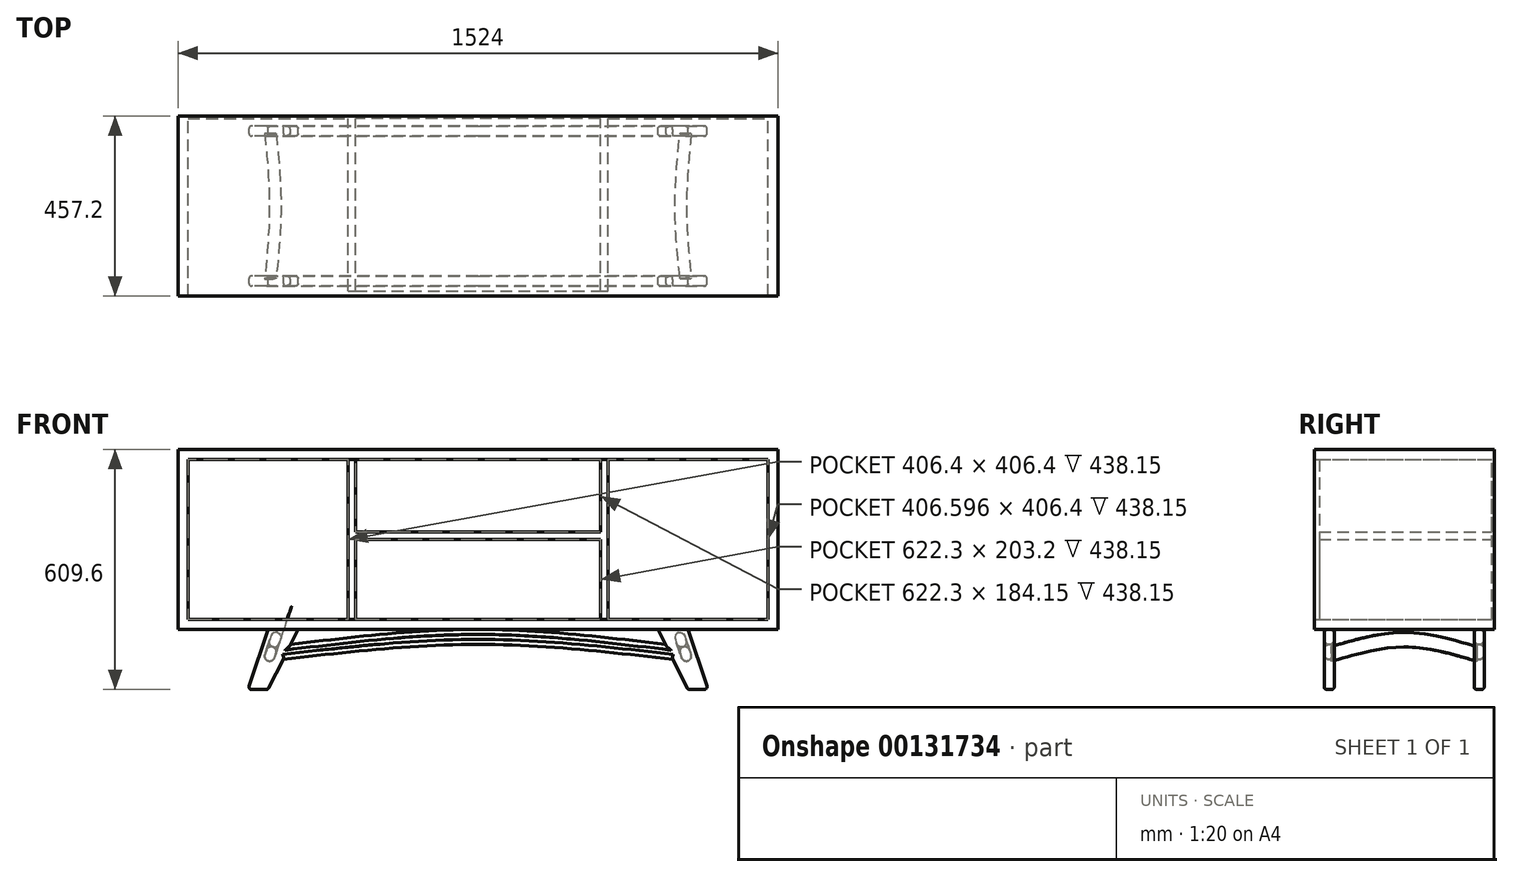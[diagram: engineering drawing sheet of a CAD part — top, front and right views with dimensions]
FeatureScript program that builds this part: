
annotation { "Feature Type Name" : "Feature", "Feature Type Description" : "" }
export const myFeature = defineFeature(function(context is Context, id is Id, definition is map)
    precondition{}
    {
        {
            var Q0;
            Q0=qCreatedBy(makeId("Front.planeOp"),FACE);
            var sketch = newSketch(context, id + "F0", { "sketchPlane" : qUnion([Q0])});
            skLineSegment(sketch, "E0.bottom", {"start": v(-762, 12.7) * mm, "end": v(762, 12.7) * mm});
            skLineSegment(sketch, "E0.top", {"start": v(-762, -12.7) * mm, "end": v(762, -12.7) * mm});
            skLineSegment(sketch, "E0.left", {"start": v(-762, 12.7) * mm, "end": v(-762, -12.7) * mm});
            skLineSegment(sketch, "E0.right", {"start": v(762, 12.7) * mm, "end": v(762, -12.7) * mm});
            skPoint(sketch, "E0.middle", {"position": v(0, 0) * mm});
            skPoint(sketch, "E1.middle", {"position": v(-348.2, 0) * mm});
            skSolve(sketch);
        }
        {
            var Q0;
            Q0=makeQuery(id+"F0.imprint","IMPRINT",FACE,{"disambiguationData":[TD([[makeQuery(id+"F0.imprint","IMPRINT",EDGE,{"derivedFrom":sQuery(id+"F0.wireOp",EDGE,"E0.bottom")}),-1.0]])]});
            extrude(context, id + "F1", {"entities" : qUnion([Q0]), "depth" : 457.2 * mm});
        }
        {
            var Q0;
            Q0=makeQuery(id+"F1.opExtrude","SWEPT_BODY",BODY,{"disambiguationData":[OSD([sQuery(id+"F0.wireOp",EDGE,"E0.bottom"),sQuery(id+"F0.wireOp",EDGE,"E0.top"),sQuery(id+"F0.wireOp",EDGE,"E0.left"),sQuery(id+"F0.wireOp",EDGE,"E0.right")])]});
            transform(context, id + "F2", {"entities" : qUnion([Q0]), "transformType" : TransformType.TRANSLATION_3D, "dx" : 0 * mm, "dy" : 0 * mm, "dz" : 0 * mm, "makeCopy" : true});
        }
        {
            var Q0;
            Q0=makeQuery(id+"F2.opPattern","COPY",EDGE,{"derivedFrom":makeQuery(id+"F1.opExtrude","SWEPT_EDGE",EDGE,{"disambiguationData":[OSD([sQuery(id+"F0.wireOp",EDGE,"E0.top"),sQuery(id+"F0.wireOp",EDGE,"E0.left")])]}),"instanceName":"1"});
            var Q1;
            Q1=makeQuery(id+"F2.opPattern","COPY",EDGE,{"derivedFrom":makeQuery(id+"F1.opExtrude","SWEPT_EDGE",EDGE,{"disambiguationData":[OSD([sQuery(id+"F0.wireOp",EDGE,"E0.top"),sQuery(id+"F0.wireOp",EDGE,"E0.right")])]}),"instanceName":"1"});
            chamfer(context, id + "F3", {"entities" : qUnion([Q0, Q1]), "width" : 25.4 * mm, "tangentPropagation" : true});
        }
        {
            var Q0;
            Q0=makeQuery(id+"F1.opExtrude","SWEPT_BODY",BODY,{"disambiguationData":[OSD([sQuery(id+"F0.wireOp",EDGE,"E0.bottom"),sQuery(id+"F0.wireOp",EDGE,"E0.top"),sQuery(id+"F0.wireOp",EDGE,"E0.left"),sQuery(id+"F0.wireOp",EDGE,"E0.right")])]});
            deleteBodies(context, id + "F4", {"entities" : qUnion([Q0])});
        }
        {
            var Q0;
            Q0=makeQuery(id+"F2.opPattern","COPY",BODY,{"derivedFrom":makeQuery(id+"F1.opExtrude","SWEPT_BODY",BODY,{"disambiguationData":[OSD([sQuery(id+"F0.wireOp",EDGE,"E0.bottom"),sQuery(id+"F0.wireOp",EDGE,"E0.top"),sQuery(id+"F0.wireOp",EDGE,"E0.left"),sQuery(id+"F0.wireOp",EDGE,"E0.right")])]}),"instanceName":"1"});
            deleteBodies(context, id + "F5", {"entities" : qUnion([Q0])});
        }
        {
            var Q0;
            Q0=qCreatedBy(makeId("Front.planeOp"),FACE);
            var sketch = newSketch(context, id + "F6", { "sketchPlane" : qUnion([Q0])});
            skLineSegment(sketch, "E2.bottom", {"start": v(762, 228.6) * mm, "end": v(-762, 228.6) * mm});
            skLineSegment(sketch, "E2.top", {"start": v(762, -228.6) * mm, "end": v(-762, -228.6) * mm});
            skLineSegment(sketch, "E2.left", {"start": v(762, 228.6) * mm, "end": v(762, -228.6) * mm});
            skLineSegment(sketch, "E2.right", {"start": v(-762, 228.6) * mm, "end": v(-762, -228.6) * mm});
            skPoint(sketch, "E2.middle", {"position": v(0, 0) * mm});
            skLineSegment(sketch, "E3.bottom", {"start": v(-736.6, 203.2) * mm, "end": v(-330.2, 203.2) * mm});
            skLineSegment(sketch, "E3.top", {"start": v(-736.6, -203.2) * mm, "end": v(-330.2, -203.2) * mm});
            skLineSegment(sketch, "E3.left", {"start": v(-736.6, 203.2) * mm, "end": v(-736.6, -203.2) * mm});
            skLineSegment(sketch, "E3.right", {"start": v(-330.2, 203.2) * mm, "end": v(-330.2, -203.2) * mm});
            skLineSegment(sketch, "E4.bottom", {"start": v(736.6, 203.2) * mm, "end": v(330.2, 203.2) * mm});
            skLineSegment(sketch, "E4.top", {"start": v(736.6, -203.2) * mm, "end": v(330, -203.2) * mm});
            skLineSegment(sketch, "E4.left", {"start": v(736.6, 203.2) * mm, "end": v(736.6, -203.2) * mm});
            skLineSegment(sketch, "E4.right", {"start": v(330.2, 203.2) * mm, "end": v(330, -203.2) * mm});
            skLineSegment(sketch, "E5.bottom", {"start": v(311.15, 203.2) * mm, "end": v(-311.15, 203.2) * mm});
            skLineSegment(sketch, "E5.top", {"start": v(311.15, -203.2) * mm, "end": v(-311.15, -203.2) * mm});
            skLineSegment(sketch, "E5.left", {"start": v(311.15, 203.2) * mm, "end": v(311.15, 19.05) * mm});
            skLineSegment(sketch, "E5.right", {"start": v(-311.15, 203.2) * mm, "end": v(-311.15, 19.05) * mm});
            skLineSegment(sketch, "E6", {"start": v(-311.15, 0) * mm, "end": v(311.15, 0) * mm});
            skLineSegment(sketch, "E7", {"start": v(311.15, 19.05) * mm, "end": v(-311.15, 19.05) * mm});
            skLineSegment(sketch, "E8", {"start": v(-311.15, 0) * mm, "end": v(-311.15, -203.2) * mm});
            skLineSegment(sketch, "E9", {"start": v(311.15, 0) * mm, "end": v(311.15, -203.2) * mm});
            skLineSegment(sketch, "E10", {"start": v(311.15, 19.05) * mm, "end": v(311.15, 19.05) * mm});
            skLineSegment(sketch, "E11", {"start": v(-533.4, -228.6) * mm, "end": v(-581.41, -372.64) * mm});
            skPoint(sketch, "E11.startSnap0", {"position": v(-533.4, -203.2) * mm});
            skLineSegment(sketch, "E12", {"start": v(533.3, -228.6) * mm, "end": v(581.32, -372.64) * mm});
            skPoint(sketch, "E12.startSnap0", {"position": v(533.3, -203.2) * mm});
            skLineSegment(sketch, "E13", {"start": v(-533.4, -381) * mm, "end": v(-575.39, -381) * mm});
            skLineSegment(sketch, "E14", {"start": v(575.3, -381) * mm, "end": v(533.3, -381) * mm});
            skLineSegment(sketch, "E15", {"start": v(533.3, -381) * mm, "end": v(495.2, -304.8) * mm});
            skLineSegment(sketch, "E16", {"start": v(-533.4, -381) * mm, "end": v(-495.3, -304.8) * mm});
            skLineSegment(sketch, "E17", {"start": v(0, -228.6) * mm, "end": v(0, -304.8) * mm});
            skPoint(sketch, "E17.endSnap0", {"position": v(-495.3, -304.8) * mm});
            skFitSpline(sketch, "E18", {"points": [v(-495.3, -304.8) * mm, v(0, -266.7) * mm, v(495.2, -304.8) * mm], "startDerivative": vector(990.58, 114.3) * mm, "endDerivative": vector(990.43, -114.3) * mm});
            skLineSegment(sketch, "E19", {"start": v(-495.3, -304.8) * mm, "end": v(-457.2, -228.6) * mm});
            skLineSegment(sketch, "E20", {"start": v(495.2, -304.8) * mm, "end": v(457.1, -228.6) * mm});
            skFitSpline(sketch, "E21", {"points": [v(-476.25, -266.7) * mm, v(0, -228.6) * mm, v(476.15, -266.7) * mm], "startDerivative": vector(952.48, 114.3) * mm, "endDerivative": vector(952.33, -114.3) * mm});
            skPoint(sketch, "E22.visualSharp", {"position": v(-584.2, -381) * mm});
            skArc(sketch, "E22.filletArc", {"start": v(-581.41, -372.64) * mm, "mid": v(-580.54, -378.36) * mm, "end": v(-575.39, -381) * mm});
            skPoint(sketch, "E23.visualSharp", {"position": v(584.1, -381) * mm});
            skArc(sketch, "E23.filletArc", {"start": v(575.3, -381) * mm, "mid": v(580.44, -378.36) * mm, "end": v(581.32, -372.64) * mm});
            skSolve(sketch);
        }
        {
            var Q0;
            Q0=makeQuery(id+"F6.imprint","IMPRINT",FACE,{"disambiguationData":[TD([[makeQuery(id+"F6.imprint","IMPRINT",EDGE,{"derivedFrom":sQuery(id+"F6.wireOp",EDGE,"E2.bottom")}),1.0]])]});
            extrude(context, id + "F7", {"entities" : qUnion([Q0]), "depth" : 457.2 * mm});
        }
        {
            var Q0;
            {var subQ1=sQuery(id+"F6.wireOp",EDGE,"E11");Q0=makeQuery(id+"F6.imprint","IMPRINT",FACE,{"disambiguationData":[TD([[makeQuery(id+"F6.imprint","IMPRINT",EDGE,{"derivedFrom":subQ1}),1.0]])]});}
            var Q1;
            {var subQ1=sQuery(id+"F6.wireOp",EDGE,"E17");var subQ3=sQuery(id+"F6.wireOp",EDGE,"E18");var subQ4=makeQuery(id+"F6.imprint","INTERSECT",VERTEX,{"derivedFrom":[subQ1,subQ3]});Q1=makeQuery(id+"F6.imprint","IMPRINT",FACE,{"disambiguationData":[TD([[makeQuery(id+"F6.imprint","IMPRINT",EDGE,{"disambiguationData":[TD([[subQ4,1.0]])],"derivedFrom":subQ1}),-1.0]])]});}
            var Q2;
            {var subQ1=sQuery(id+"F6.wireOp",EDGE,"E17");var subQ3=sQuery(id+"F6.wireOp",EDGE,"E18");var subQ4=makeQuery(id+"F6.imprint","INTERSECT",VERTEX,{"derivedFrom":[subQ1,subQ3]});Q2=makeQuery(id+"F6.imprint","IMPRINT",FACE,{"disambiguationData":[TD([[makeQuery(id+"F6.imprint","IMPRINT",EDGE,{"disambiguationData":[TD([[subQ4,1.0]])],"derivedFrom":subQ1}),1.0]])]});}
            var Q3;
            {var subQ0=sQuery(id+"F6.wireOp",EDGE,"E12");Q3=makeQuery(id+"F6.imprint","IMPRINT",FACE,{"disambiguationData":[TD([[makeQuery(id+"F6.imprint","IMPRINT",EDGE,{"derivedFrom":subQ0}),-1.0]])]});}
            extrude(context, id + "F8", {"entities" : qUnion([Q0, Q1, Q2, Q3]), "depth" : 50.8 * mm, "hasSecondDirection" : true, "secondDirectionOppositeDirection" : false, "secondDirectionDepth" : 25.4 * mm});
        }
        {
            var Q0;
            {var subQ1=sQuery(id+"F6.wireOp",EDGE,"E11");Q0=makeQuery(id+"F6.imprint","IMPRINT",FACE,{"disambiguationData":[TD([[makeQuery(id+"F6.imprint","IMPRINT",EDGE,{"derivedFrom":subQ1}),1.0]])]});}
            var Q1;
            {var subQ1=sQuery(id+"F6.wireOp",EDGE,"E17");var subQ3=sQuery(id+"F6.wireOp",EDGE,"E18");var subQ4=makeQuery(id+"F6.imprint","INTERSECT",VERTEX,{"derivedFrom":[subQ1,subQ3]});Q1=makeQuery(id+"F6.imprint","IMPRINT",FACE,{"disambiguationData":[TD([[makeQuery(id+"F6.imprint","IMPRINT",EDGE,{"disambiguationData":[TD([[subQ4,1.0]])],"derivedFrom":subQ1}),-1.0]])]});}
            var Q2;
            {var subQ1=sQuery(id+"F6.wireOp",EDGE,"E17");var subQ3=sQuery(id+"F6.wireOp",EDGE,"E18");var subQ4=makeQuery(id+"F6.imprint","INTERSECT",VERTEX,{"derivedFrom":[subQ1,subQ3]});Q2=makeQuery(id+"F6.imprint","IMPRINT",FACE,{"disambiguationData":[TD([[makeQuery(id+"F6.imprint","IMPRINT",EDGE,{"disambiguationData":[TD([[subQ4,1.0]])],"derivedFrom":subQ1}),1.0]])]});}
            var Q3;
            {var subQ0=sQuery(id+"F6.wireOp",EDGE,"E12");Q3=makeQuery(id+"F6.imprint","IMPRINT",FACE,{"disambiguationData":[TD([[makeQuery(id+"F6.imprint","IMPRINT",EDGE,{"derivedFrom":subQ0}),-1.0]])]});}
            extrude(context, id + "F9", {"entities" : qUnion([Q0, Q1, Q2, Q3]), "depth" : 431.8 * mm, "hasSecondDirection" : true, "secondDirectionOppositeDirection" : false, "secondDirectionDepth" : 406.4 * mm});
        }
        {
            var Q0;
            Q0=makeQuery(id+"F7.opExtrude","CAP_FACE",FACE,{"disambiguationData":[OSD([sQuery(id+"F6.wireOp",EDGE,"E2.bottom"),sQuery(id+"F6.wireOp",EDGE,"E2.top"),sQuery(id+"F6.wireOp",EDGE,"E2.left"),sQuery(id+"F6.wireOp",EDGE,"E2.right"),sQuery(id+"F6.wireOp",EDGE,"E3.bottom"),sQuery(id+"F6.wireOp",EDGE,"E3.top"),sQuery(id+"F6.wireOp",EDGE,"E3.left"),sQuery(id+"F6.wireOp",EDGE,"E3.right"),sQuery(id+"F6.wireOp",EDGE,"E4.bottom"),sQuery(id+"F6.wireOp",EDGE,"E4.top"),sQuery(id+"F6.wireOp",EDGE,"E4.left"),sQuery(id+"F6.wireOp",EDGE,"E4.right"),sQuery(id+"F6.wireOp",EDGE,"E5.bottom"),sQuery(id+"F6.wireOp",EDGE,"E5.top"),sQuery(id+"F6.wireOp",EDGE,"E5.left"),sQuery(id+"F6.wireOp",EDGE,"E5.right"),sQuery(id+"F6.wireOp",EDGE,"E6"),sQuery(id+"F6.wireOp",EDGE,"E7"),sQuery(id+"F6.wireOp",EDGE,"E8"),sQuery(id+"F6.wireOp",EDGE,"E9")])],"isStart":false});
            var sketch = newSketch(context, id + "F10", { "sketchPlane" : qUnion([Q0])});
            skLineSegment(sketch, "E24", {"start": v(-330.2, 203.2) * mm, "end": v(-311.15, 203.2) * mm});
            skLineSegment(sketch, "E25", {"start": v(311.15, 203.2) * mm, "end": v(330.2, 203.2) * mm});
            skLineSegment(sketch, "E26", {"start": v(-330.2, -203.2) * mm, "end": v(-311.15, -203.2) * mm});
            skLineSegment(sketch, "E27", {"start": v(311.15, -203.2) * mm, "end": v(330, -203.2) * mm});
            skSolve(sketch);
        }
        {
            var Q0;
            Q0=makeQuery(id+"F10.imprint","IMPRINT",FACE,{"disambiguationData":[TD([[makeQuery(id+"F10.imprint","IMPRINT",EDGE,{"derivedFrom":sQuery(id+"F10.wireOp",EDGE,"E24")}),-1.0]])]});
            extrude(context, id + "F11", {"entities" : qUnion([Q0]), "operationType" : NewBodyOperationType.REMOVE, "oppositeDirection" : true, "depth" : 12.7 * mm});
        }
        {
            var Q0;
            Q0=makeQuery(id+"F9.opExtrude","CAP_EDGE",EDGE,{"disambiguationData":[OSD([sQuery(id+"F6.wireOp",EDGE,"E11")])],"isStart":false});
            var Q1;
            Q1=makeQuery(id+"F9.opExtrude","CAP_EDGE",EDGE,{"disambiguationData":[OSD([sQuery(id+"F6.wireOp",EDGE,"E16")])],"isStart":false});
            var Q2;
            Q2=makeQuery(id+"F9.opExtrude","CAP_EDGE",EDGE,{"disambiguationData":[OSD([sQuery(id+"F6.wireOp",EDGE,"E15")])],"isStart":false});
            var Q3;
            Q3=makeQuery(id+"F9.opExtrude","CAP_EDGE",EDGE,{"disambiguationData":[OSD([sQuery(id+"F6.wireOp",EDGE,"E12")])],"isStart":false});
            var Q4;
            Q4=makeQuery(id+"F9.opExtrude","CAP_EDGE",EDGE,{"disambiguationData":[OSD([sQuery(id+"F6.wireOp",EDGE,"E12")])],"isStart":true});
            var Q5;
            Q5=makeQuery(id+"F9.opExtrude","CAP_EDGE",EDGE,{"disambiguationData":[OSD([sQuery(id+"F6.wireOp",EDGE,"E20")])],"isStart":false});
            var Q6;
            Q6=makeQuery(id+"F9.opExtrude","CAP_EDGE",EDGE,{"disambiguationData":[OSD([sQuery(id+"F6.wireOp",EDGE,"E19")])],"isStart":false});
            var Q7;
            Q7=makeQuery(id+"F9.opExtrude","CAP_EDGE",EDGE,{"disambiguationData":[OSD([sQuery(id+"F6.wireOp",EDGE,"E15")])],"isStart":true});
            var Q8;
            Q8=makeQuery(id+"F9.opExtrude","CAP_EDGE",EDGE,{"disambiguationData":[OSD([sQuery(id+"F6.wireOp",EDGE,"E20")])],"isStart":true});
            var Q9;
            Q9=makeQuery(id+"F9.opExtrude","CAP_EDGE",EDGE,{"disambiguationData":[OSD([sQuery(id+"F6.wireOp",EDGE,"E16")])],"isStart":true});
            var Q10;
            Q10=makeQuery(id+"F9.opExtrude","CAP_EDGE",EDGE,{"disambiguationData":[OSD([sQuery(id+"F6.wireOp",EDGE,"E11")])],"isStart":true});
            var Q11;
            Q11=makeQuery(id+"F9.opExtrude","CAP_EDGE",EDGE,{"disambiguationData":[OSD([sQuery(id+"F6.wireOp",EDGE,"E19")])],"isStart":true});
            var Q12;
            Q12=makeQuery(id+"F8.opExtrude","CAP_EDGE",EDGE,{"disambiguationData":[OSD([sQuery(id+"F6.wireOp",EDGE,"E12")])],"isStart":true});
            var Q13;
            Q13=makeQuery(id+"F8.opExtrude","CAP_EDGE",EDGE,{"disambiguationData":[OSD([sQuery(id+"F6.wireOp",EDGE,"E20")])],"isStart":true});
            var Q14;
            Q14=makeQuery(id+"F8.opExtrude","CAP_EDGE",EDGE,{"disambiguationData":[OSD([sQuery(id+"F6.wireOp",EDGE,"E15")])],"isStart":true});
            var Q15;
            Q15=makeQuery(id+"F8.opExtrude","CAP_EDGE",EDGE,{"disambiguationData":[OSD([sQuery(id+"F6.wireOp",EDGE,"E16")])],"isStart":false});
            var Q16;
            Q16=makeQuery(id+"F8.opExtrude","CAP_EDGE",EDGE,{"disambiguationData":[OSD([sQuery(id+"F6.wireOp",EDGE,"E11")])],"isStart":true});
            var Q17;
            Q17=makeQuery(id+"F8.opExtrude","CAP_EDGE",EDGE,{"disambiguationData":[OSD([sQuery(id+"F6.wireOp",EDGE,"E16")])],"isStart":true});
            var Q18;
            Q18=makeQuery(id+"F8.opExtrude","CAP_EDGE",EDGE,{"disambiguationData":[OSD([sQuery(id+"F6.wireOp",EDGE,"E19")])],"isStart":true});
            var Q19;
            Q19=makeQuery(id+"F8.opExtrude","CAP_EDGE",EDGE,{"disambiguationData":[OSD([sQuery(id+"F6.wireOp",EDGE,"E11")])],"isStart":false});
            var Q20;
            Q20=makeQuery(id+"F8.opExtrude","CAP_EDGE",EDGE,{"disambiguationData":[OSD([sQuery(id+"F6.wireOp",EDGE,"E19")])],"isStart":false});
            var Q21;
            Q21=makeQuery(id+"F8.opExtrude","CAP_EDGE",EDGE,{"disambiguationData":[OSD([sQuery(id+"F6.wireOp",EDGE,"E12")])],"isStart":false});
            var Q22;
            Q22=makeQuery(id+"F8.opExtrude","CAP_EDGE",EDGE,{"disambiguationData":[OSD([sQuery(id+"F6.wireOp",EDGE,"E20")])],"isStart":false});
            var Q23;
            Q23=makeQuery(id+"F8.opExtrude","CAP_EDGE",EDGE,{"disambiguationData":[OSD([sQuery(id+"F6.wireOp",EDGE,"E15")])],"isStart":false});
            var Q24;
            Q24=makeQuery(id+"F9.opExtrude","CAP_EDGE",EDGE,{"disambiguationData":[OSD([sQuery(id+"F6.wireOp",EDGE,"E14")])],"isStart":false});
            var Q25;
            Q25=makeQuery(id+"F9.opExtrude","CAP_EDGE",EDGE,{"disambiguationData":[OSD([sQuery(id+"F6.wireOp",EDGE,"E14")])],"isStart":true});
            var Q26;
            Q26=makeQuery(id+"F8.opExtrude","CAP_EDGE",EDGE,{"disambiguationData":[OSD([sQuery(id+"F6.wireOp",EDGE,"E14")])],"isStart":true});
            var Q27;
            Q27=makeQuery(id+"F8.opExtrude","SWEPT_EDGE",EDGE,{"disambiguationData":[OSD([sQuery(id+"F6.wireOp",EDGE,"E14"),sQuery(id+"F6.wireOp",EDGE,"E15")])]});
            var Q28;
            Q28=makeQuery(id+"F9.opExtrude","CAP_EDGE",EDGE,{"disambiguationData":[OSD([sQuery(id+"F6.wireOp",EDGE,"E13")])],"isStart":false});
            var Q29;
            Q29=makeQuery(id+"F9.opExtrude","CAP_EDGE",EDGE,{"disambiguationData":[OSD([sQuery(id+"F6.wireOp",EDGE,"E13")])],"isStart":true});
            var Q30;
            Q30=makeQuery(id+"F8.opExtrude","CAP_EDGE",EDGE,{"disambiguationData":[OSD([sQuery(id+"F6.wireOp",EDGE,"E13")])],"isStart":false});
            var Q31;
            Q31=makeQuery(id+"F8.opExtrude","CAP_EDGE",EDGE,{"disambiguationData":[OSD([sQuery(id+"F6.wireOp",EDGE,"E13")])],"isStart":true});
            var Q32;
            Q32=makeQuery(id+"F9.opExtrude","SWEPT_EDGE",EDGE,{"disambiguationData":[OSD([sQuery(id+"F6.wireOp",EDGE,"E14"),sQuery(id+"F6.wireOp",EDGE,"E15")])]});
            var Q33;
            Q33=makeQuery(id+"F9.opExtrude","SWEPT_EDGE",EDGE,{"disambiguationData":[OSD([sQuery(id+"F6.wireOp",EDGE,"E13"),sQuery(id+"F6.wireOp",EDGE,"E16")])]});
            var Q34;
            Q34=makeQuery(id+"F8.opExtrude","SWEPT_EDGE",EDGE,{"disambiguationData":[OSD([sQuery(id+"F6.wireOp",EDGE,"E13"),sQuery(id+"F6.wireOp",EDGE,"E16")])]});
            fillet(context, id + "F12", {"entities" : qUnion([Q0, Q1, Q2, Q3, Q4, Q5, Q6, Q7, Q8, Q9, Q10, Q11, Q12, Q13, Q14, Q15, Q16, Q17, Q18, Q19, Q20, Q21, Q22, Q23, Q24, Q25, Q26, Q27, Q28, Q29, Q30, Q31, Q32, Q33, Q34]), "radius" : 6.35 * mm, "tangentPropagation" : true, "allowEdgeOverflow" : false});
        }
        {
            var Q0;
            Q0=makeQuery(id+"F9.opExtrude","CAP_EDGE",EDGE,{"disambiguationData":[OSD([sQuery(id+"F6.wireOp",EDGE,"E21")])],"isStart":false});
            var Q1;
            Q1=makeQuery(id+"F9.opExtrude","CAP_EDGE",EDGE,{"disambiguationData":[OSD([sQuery(id+"F6.wireOp",EDGE,"E18")])],"isStart":false});
            var Q2;
            Q2=makeQuery(id+"F8.opExtrude","CAP_EDGE",EDGE,{"disambiguationData":[OSD([sQuery(id+"F6.wireOp",EDGE,"E18")])],"isStart":false});
            var Q3;
            Q3=makeQuery(id+"F8.opExtrude","CAP_EDGE",EDGE,{"disambiguationData":[OSD([sQuery(id+"F6.wireOp",EDGE,"E18")])],"isStart":true});
            var Q4;
            Q4=makeQuery(id+"F8.opExtrude","CAP_EDGE",EDGE,{"disambiguationData":[OSD([sQuery(id+"F6.wireOp",EDGE,"E21")])],"isStart":false});
            var Q5;
            Q5=makeQuery(id+"F9.opExtrude","CAP_EDGE",EDGE,{"disambiguationData":[OSD([sQuery(id+"F6.wireOp",EDGE,"E21")])],"isStart":true});
            var Q6;
            Q6=makeQuery(id+"F9.opExtrude","CAP_EDGE",EDGE,{"disambiguationData":[OSD([sQuery(id+"F6.wireOp",EDGE,"E18")])],"isStart":true});
            var Q7;
            Q7=makeQuery(id+"F8.opExtrude","CAP_EDGE",EDGE,{"disambiguationData":[OSD([sQuery(id+"F6.wireOp",EDGE,"E21")])],"isStart":true});
            fillet(context, id + "F13", {"entities" : qUnion([Q0, Q1, Q2, Q3, Q4, Q5, Q6, Q7]), "radius" : 12.7 * mm, "tangentPropagation" : true, "allowEdgeOverflow" : false});
        }
        {
            var Q0;
            Q0=makeQuery(id+"F8.opExtrude","SWEPT_FACE",FACE,{"disambiguationData":[OSD([sQuery(id+"F6.wireOp",EDGE,"E11")])]});
            var sketch = newSketch(context, id + "F14", { "sketchPlane" : qUnion([Q0])});
            skPoint(sketch, "E28.endSnap0", {"position": v(44.45, -461.46) * mm});
            skFitSpline(sketch, "E29", {"points": [v(44.45, -461.46) * mm, v(228.69, -423.5) * mm, v(413.45, -461.46) * mm], "startDerivative": vector(368.59, 113.9) * mm, "endDerivative": vector(369.4, -113.85) * mm});
            skFitSpline(sketch, "E30", {"points": [v(44.45, -423.5) * mm, v(228.69, -385.54) * mm, v(413.19, -423.5) * mm], "startDerivative": vector(368.53, 113.89) * mm, "endDerivative": vector(368.94, -113.86) * mm});
            skLineSegment(sketch, "E31", {"start": v(44.45, -423.5) * mm, "end": v(44.45, -461.46) * mm});
            skLineSegment(sketch, "E32", {"start": v(413.19, -423.5) * mm, "end": v(413.45, -461.46) * mm});
            skSolve(sketch);
        }
        {
            var Q0;
            Q0=makeQuery(id+"F14.imprint","IMPRINT",FACE,{"disambiguationData":[TD([[makeQuery(id+"F14.imprint","IMPRINT",EDGE,{"derivedFrom":sQuery(id+"F14.wireOp",EDGE,"E29")}),1.0]])]});
            extrude(context, id + "F15", {"entities" : qUnion([Q0]), "oppositeDirection" : true, "depth" : 38.1 * mm, "hasSecondDirection" : true, "secondDirectionOppositeDirection" : true, "secondDirectionDepth" : 12.7 * mm});
        }
        {
            var Q0;
            Q0=makeQuery(id+"F9.opExtrude","SWEPT_FACE",FACE,{"disambiguationData":[OSD([sQuery(id+"F6.wireOp",EDGE,"E12")])]});
            var sketch = newSketch(context, id + "F16", { "sketchPlane" : qUnion([Q0])});
            skLineSegment(sketch, "E33", {"start": v(-44.45, -461.43) * mm, "end": v(-44.45, -423.47) * mm});
            skFitSpline(sketch, "E34", {"points": [v(-412.75, -423.47) * mm, v(-228.6, -385.51) * mm, v(-44.45, -423.47) * mm], "startDerivative": vector(368.3, 113.88) * mm, "endDerivative": vector(368.3, -113.88) * mm});
            skFitSpline(sketch, "E35", {"points": [v(-44.45, -461.43) * mm, v(-228.6, -423.47) * mm, v(-412.75, -461.43) * mm], "startDerivative": vector(-368.3, 113.88) * mm, "endDerivative": vector(-368.3, -113.88) * mm});
            skLineSegment(sketch, "E36", {"start": v(-412.75, -423.47) * mm, "end": v(-412.75, -461.43) * mm});
            skSolve(sketch);
        }
        {
            var Q0;
            Q0=makeQuery(id+"F16.imprint","IMPRINT",FACE,{"disambiguationData":[TD([[makeQuery(id+"F16.imprint","IMPRINT",EDGE,{"derivedFrom":sQuery(id+"F16.wireOp",EDGE,"E33")}),1.0]])]});
            extrude(context, id + "F17", {"entities" : qUnion([Q0]), "oppositeDirection" : true, "depth" : 38.1 * mm, "hasSecondDirection" : true, "secondDirectionOppositeDirection" : true, "secondDirectionDepth" : 12.7 * mm});
        }
        {
            var Q0;
            Q0=makeQuery(id+"F17.opExtrude","CAP_EDGE",EDGE,{"disambiguationData":[OSD([sQuery(id+"F16.wireOp",EDGE,"E35")])],"isStart":true});
            var Q1;
            Q1=makeQuery(id+"F17.opExtrude","CAP_EDGE",EDGE,{"disambiguationData":[OSD([sQuery(id+"F16.wireOp",EDGE,"E35")])],"isStart":false});
            var Q2;
            Q2=makeQuery(id+"F17.opExtrude","CAP_EDGE",EDGE,{"disambiguationData":[OSD([sQuery(id+"F16.wireOp",EDGE,"E34")])],"isStart":true});
            var Q3;
            Q3=makeQuery(id+"F15.opExtrude","CAP_EDGE",EDGE,{"disambiguationData":[OSD([sQuery(id+"F14.wireOp",EDGE,"E29")])],"isStart":false});
            var Q4;
            Q4=makeQuery(id+"F15.opExtrude","CAP_EDGE",EDGE,{"disambiguationData":[OSD([sQuery(id+"F14.wireOp",EDGE,"E30")])],"isStart":true});
            var Q5;
            Q5=makeQuery(id+"F15.opExtrude","CAP_EDGE",EDGE,{"disambiguationData":[OSD([sQuery(id+"F14.wireOp",EDGE,"E30")])],"isStart":false});
            var Q6;
            Q6=makeQuery(id+"F17.opExtrude","CAP_EDGE",EDGE,{"disambiguationData":[OSD([sQuery(id+"F16.wireOp",EDGE,"E34")])],"isStart":false});
            var Q7;
            Q7=makeQuery(id+"F15.opExtrude","CAP_EDGE",EDGE,{"disambiguationData":[OSD([sQuery(id+"F14.wireOp",EDGE,"E29")])],"isStart":true});
            fillet(context, id + "F18", {"entities" : qUnion([Q0, Q1, Q2, Q3, Q4, Q5, Q6, Q7]), "radius" : 12.7 * mm, "allowEdgeOverflow" : false});
        }
        {
            var Q0;
            Q0=makeQuery(id+"F7.opExtrude","CAP_FACE",FACE,{"disambiguationData":[OSD([sQuery(id+"F6.wireOp",EDGE,"E2.bottom"),sQuery(id+"F6.wireOp",EDGE,"E2.top"),sQuery(id+"F6.wireOp",EDGE,"E2.left"),sQuery(id+"F6.wireOp",EDGE,"E2.right"),sQuery(id+"F6.wireOp",EDGE,"E3.bottom"),sQuery(id+"F6.wireOp",EDGE,"E3.top"),sQuery(id+"F6.wireOp",EDGE,"E3.left"),sQuery(id+"F6.wireOp",EDGE,"E3.right"),sQuery(id+"F6.wireOp",EDGE,"E4.bottom"),sQuery(id+"F6.wireOp",EDGE,"E4.top"),sQuery(id+"F6.wireOp",EDGE,"E4.left"),sQuery(id+"F6.wireOp",EDGE,"E4.right"),sQuery(id+"F6.wireOp",EDGE,"E5.bottom"),sQuery(id+"F6.wireOp",EDGE,"E5.top"),sQuery(id+"F6.wireOp",EDGE,"E5.left"),sQuery(id+"F6.wireOp",EDGE,"E5.right"),sQuery(id+"F6.wireOp",EDGE,"E6"),sQuery(id+"F6.wireOp",EDGE,"E7"),sQuery(id+"F6.wireOp",EDGE,"E8"),sQuery(id+"F6.wireOp",EDGE,"E9")])],"isStart":true});
            var sketch = newSketch(context, id + "F19", { "sketchPlane" : qUnion([Q0])});
            skLineSegment(sketch, "E37.bottom", {"start": v(749.3, -215.9) * mm, "end": v(-749.3, -215.9) * mm});
            skLineSegment(sketch, "E37.top", {"start": v(749.3, 215.9) * mm, "end": v(-749.3, 215.9) * mm});
            skLineSegment(sketch, "E37.left", {"start": v(749.3, -215.9) * mm, "end": v(749.3, 215.9) * mm});
            skLineSegment(sketch, "E37.right", {"start": v(-749.3, -215.9) * mm, "end": v(-749.3, 215.9) * mm});
            skPoint(sketch, "E37.middle", {"position": v(0, 0) * mm});
            skSolve(sketch);
        }
        {
            var Q0;
            Q0 = qSketchRegion(id + "F19", true);
            extrude(context, id + "F20", {"entities" : qUnion([Q0]), "operationType" : NewBodyOperationType.ADD, "oppositeDirection" : true, "depth" : 6.35 * mm});
        }
    });
